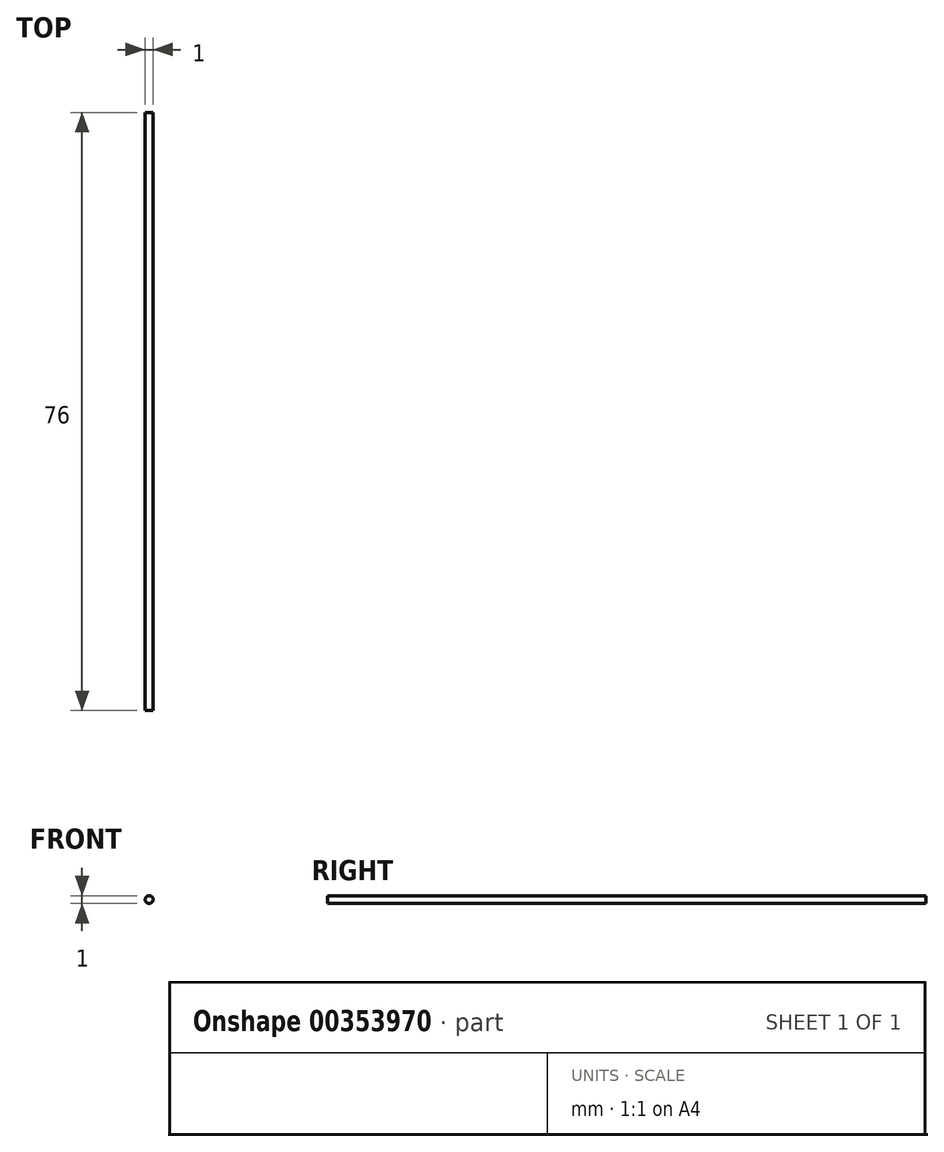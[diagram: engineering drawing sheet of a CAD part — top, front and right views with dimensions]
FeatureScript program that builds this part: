
annotation { "Feature Type Name" : "Feature", "Feature Type Description" : "" }
export const myFeature = defineFeature(function(context is Context, id is Id, definition is map)
    precondition{}
    {
        {
            var Q0;
            Q0=qCreatedBy(makeId("Front.planeOp"),FACE);
            var sketch = newSketch(context, id + "F0", { "sketchPlane" : qUnion([Q0])});
            skCircle(sketch, "E0", {"center": v(0, 0) * mm, "radius": 0.5 * mm});
            skSolve(sketch);
        }
        {
            var Q0;
            Q0=makeQuery(id+"F0.imprint","IMPRINT",FACE,{"disambiguationData":[TD([[makeQuery(id+"F0.imprint","IMPRINT",EDGE,{"derivedFrom":sQuery(id+"F0.wireOp",EDGE,"E0")}),1.0]])]});
            extrude(context, id + "F1", {"entities" : qUnion([Q0]), "endBound" : BoundingType.SYMMETRIC, "depth" : 76 * mm});
        }
    });
